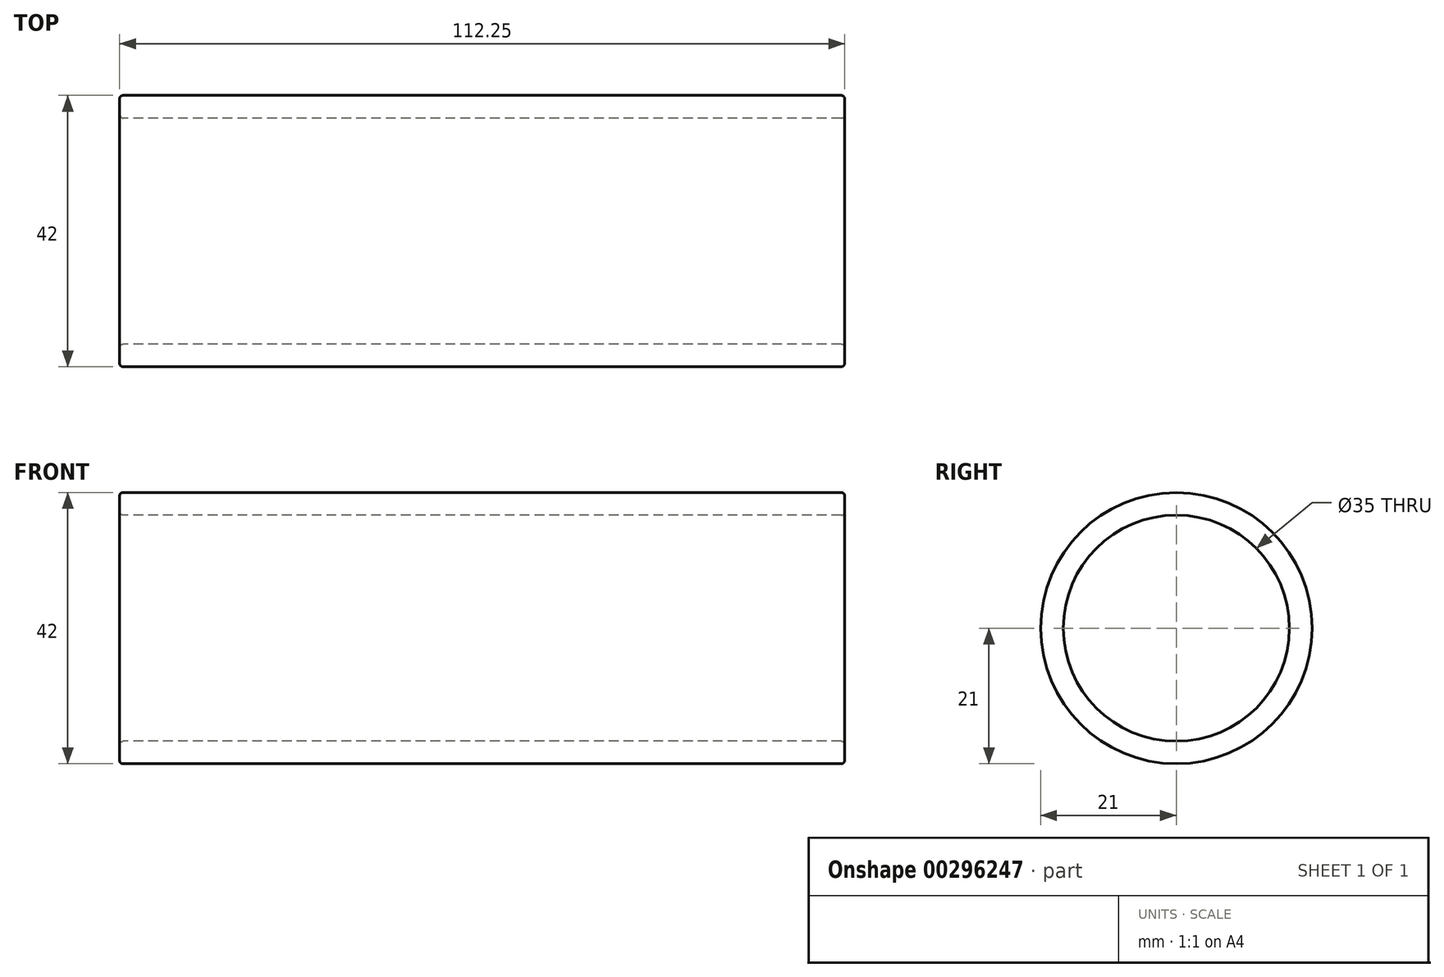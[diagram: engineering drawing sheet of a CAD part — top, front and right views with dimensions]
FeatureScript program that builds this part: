
annotation { "Feature Type Name" : "Feature", "Feature Type Description" : "" }
export const myFeature = defineFeature(function(context is Context, id is Id, definition is map)
    precondition{}
    {
        {
            var Q0;
            Q0=qCreatedBy(makeId("Front.planeOp"),FACE);
            var sketch = newSketch(context, id + "F0", { "sketchPlane" : qUnion([Q0])});
            skLineSegment(sketch, "E0.bottom", {"start": v(56.09, 17.5) * mm, "end": v(-56.09, 17.5) * mm});
            skLineSegment(sketch, "E0.top", {"start": v(56.09, -17.5) * mm, "end": v(-56.09, -17.5) * mm});
            skLineSegment(sketch, "E0.left", {"start": v(56.09, 17.5) * mm, "end": v(56.09, -17.5) * mm});
            skLineSegment(sketch, "E0.right", {"start": v(-56.09, 17.5) * mm, "end": v(-56.09, -17.5) * mm});
            skPoint(sketch, "E0.middle", {"position": v(0, 0) * mm});
            skLineSegment(sketch, "E1", {"start": v(56.09, 17.5) * mm, "end": v(56.09, 21) * mm});
            skLineSegment(sketch, "E2", {"start": v(56.09, 21) * mm, "end": v(-56.17, 21) * mm});
            skLineSegment(sketch, "E3", {"start": v(-56.17, 21) * mm, "end": v(-56.09, 17.5) * mm});
            skLineSegment(sketch, "E4", {"start": v(56.09, -17.5) * mm, "end": v(56.09, -21) * mm});
            skLineSegment(sketch, "E5", {"start": v(56.09, -21) * mm, "end": v(-56.09, -21) * mm});
            skLineSegment(sketch, "E6", {"start": v(-56.09, -21) * mm, "end": v(-56.09, -17.5) * mm});
            skLineSegment(sketch, "E7", {"start": v(-56.09, 0) * mm, "end": v(56.09, 0) * mm, "construction": true});
            skSolve(sketch);
        }
        {
            var Q0;
            Q0=makeQuery(id+"F0.imprint","IMPRINT",FACE,{"disambiguationData":[TD([[makeQuery(id+"F0.imprint","IMPRINT",EDGE,{"derivedFrom":sQuery(id+"F0.wireOp",EDGE,"E0.bottom")}),-1.0]])]});
            var Q1;
            Q1=sQuery(id+"F0.wireOp",EDGE,"E7");
            revolve(context, id + "F1", {"entities" : qUnion([Q0]), "axis" : qUnion([Q1]), "revolveType" : RevolveType.FULL});
        }
        {
            var Q0;
            Q0=makeQuery(id+"F1.opRevolve","SWEPT_EDGE",EDGE,{"disambiguationData":[OSD([sQuery(id+"F0.wireOp",EDGE,"E0.bottom"),sQuery(id+"F0.wireOp",EDGE,"E0.left"),sQuery(id+"F0.wireOp",EDGE,"E1")])]});
            var Q1;
            Q1=makeQuery(id+"F1.opRevolve","SWEPT_EDGE",EDGE,{"disambiguationData":[OSD([sQuery(id+"F0.wireOp",EDGE,"E1"),sQuery(id+"F0.wireOp",EDGE,"E2")])]});
            var Q2;
            Q2=makeQuery(id+"F1.opRevolve","SWEPT_EDGE",EDGE,{"disambiguationData":[OSD([sQuery(id+"F0.wireOp",EDGE,"E2"),sQuery(id+"F0.wireOp",EDGE,"E3")])]});
            var Q3;
            Q3=makeQuery(id+"F1.opRevolve","SWEPT_EDGE",EDGE,{"disambiguationData":[OSD([sQuery(id+"F0.wireOp",EDGE,"E0.bottom"),sQuery(id+"F0.wireOp",EDGE,"E0.right"),sQuery(id+"F0.wireOp",EDGE,"E3")])]});
            fillet(context, id + "F2", {"entities" : qUnion([Q0, Q1, Q2, Q3]), "radius" : 0.5 * mm, "tangentPropagation" : true, "allowEdgeOverflow" : false});
        }
    });
